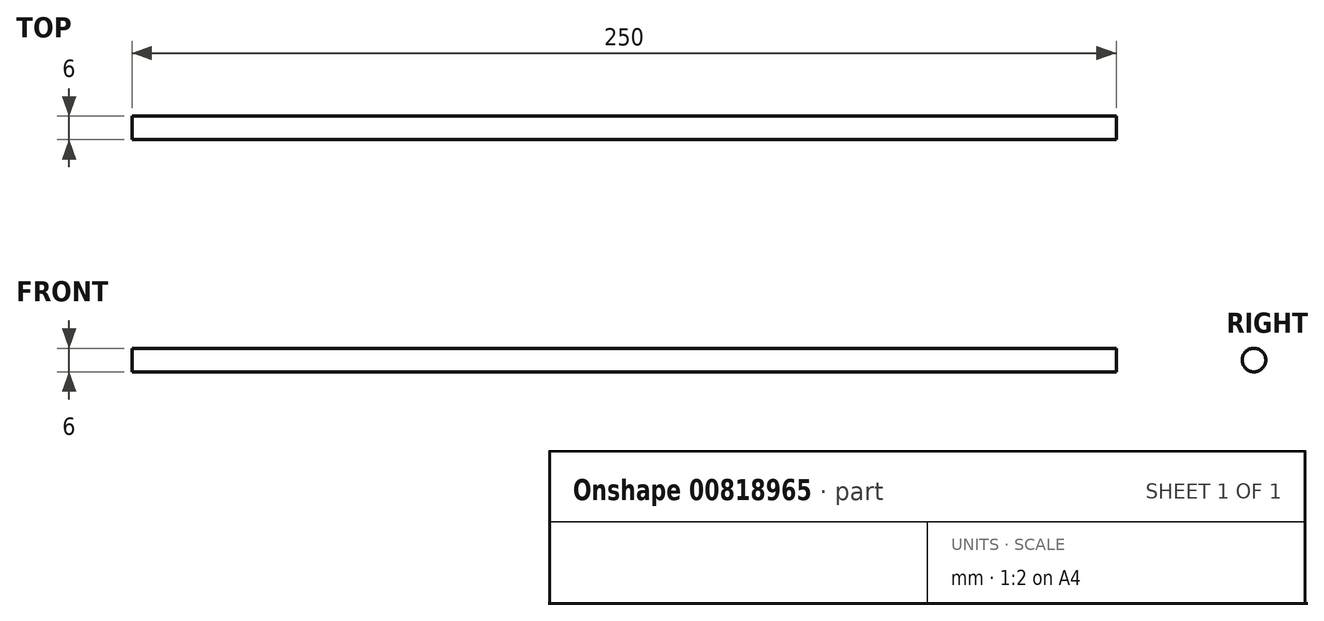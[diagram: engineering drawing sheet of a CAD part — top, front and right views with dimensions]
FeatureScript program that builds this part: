
annotation { "Feature Type Name" : "Feature", "Feature Type Description" : "" }
export const myFeature = defineFeature(function(context is Context, id is Id, definition is map)
    precondition{}
    {
        {
            var Q0;
            Q0=qCreatedBy(makeId("Right.planeOp"),FACE);
            var sketch = newSketch(context, id + "F0", { "sketchPlane" : qUnion([Q0])});
            skCircle(sketch, "E0", {"center": v(0, 0) * mm, "radius": 3 * mm});
            skSolve(sketch);
        }
        {
            var Q0;
            Q0 = qSketchRegion(id + "F0", true);
            extrude(context, id + "F1", {"entities" : qUnion([Q0]), "depth" : 250 * mm, "offsetDistance" : 25 * mm});
        }
    });
